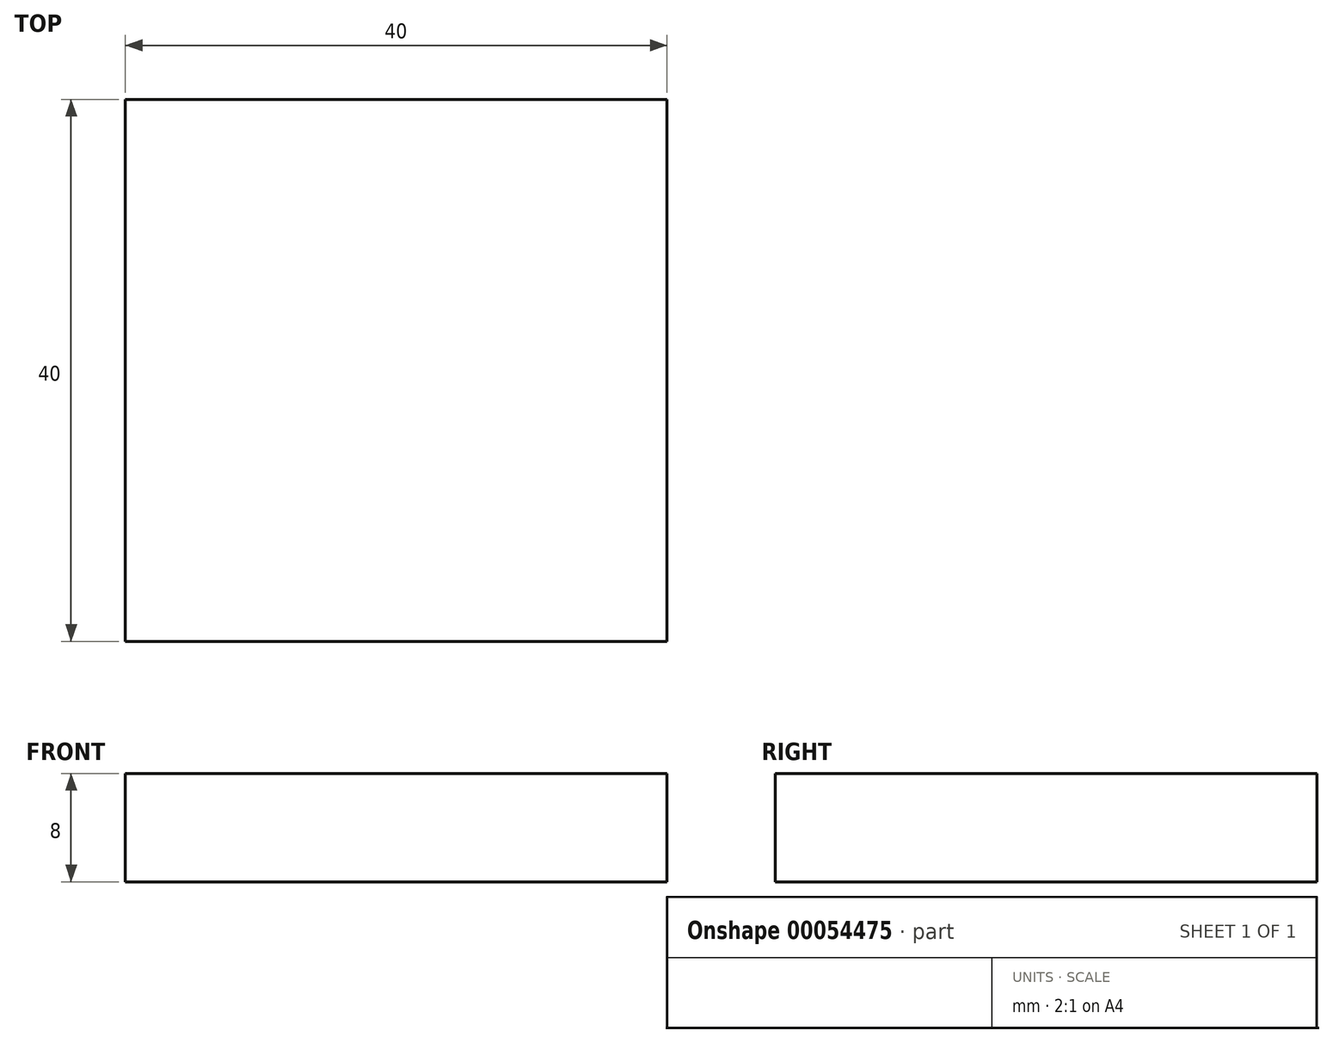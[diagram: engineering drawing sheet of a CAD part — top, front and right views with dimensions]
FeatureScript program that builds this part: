
annotation { "Feature Type Name" : "Feature", "Feature Type Description" : "" }
export const myFeature = defineFeature(function(context is Context, id is Id, definition is map)
    precondition{}
    {
        {
            var Q0;
            Q0=qCreatedBy(makeId("Top.planeOp"),FACE);
            var sketch = newSketch(context, id + "F0", { "sketchPlane" : qUnion([Q0])});
            skLineSegment(sketch, "E0.rect.bottom", {"start": v(20, -20) * mm, "end": v(-20, -20) * mm});
            skLineSegment(sketch, "E0.rect.top", {"start": v(20, 20) * mm, "end": v(-20, 20) * mm});
            skLineSegment(sketch, "E0.rect.left", {"start": v(20, -20) * mm, "end": v(20, 20) * mm});
            skLineSegment(sketch, "E0.rect.right", {"start": v(-20, -20) * mm, "end": v(-20, 20) * mm});
            skPoint(sketch, "E0.rect.middle", {"position": v(0, 0) * mm});
            skSolve(sketch);
        }
        {
            var Q0;
            Q0=qSketchRegion(id+"F0",true);
            extrude(context, id + "F1", {"entities" : qUnion([Q0]), "depth" : 8 * mm});
        }
    });
